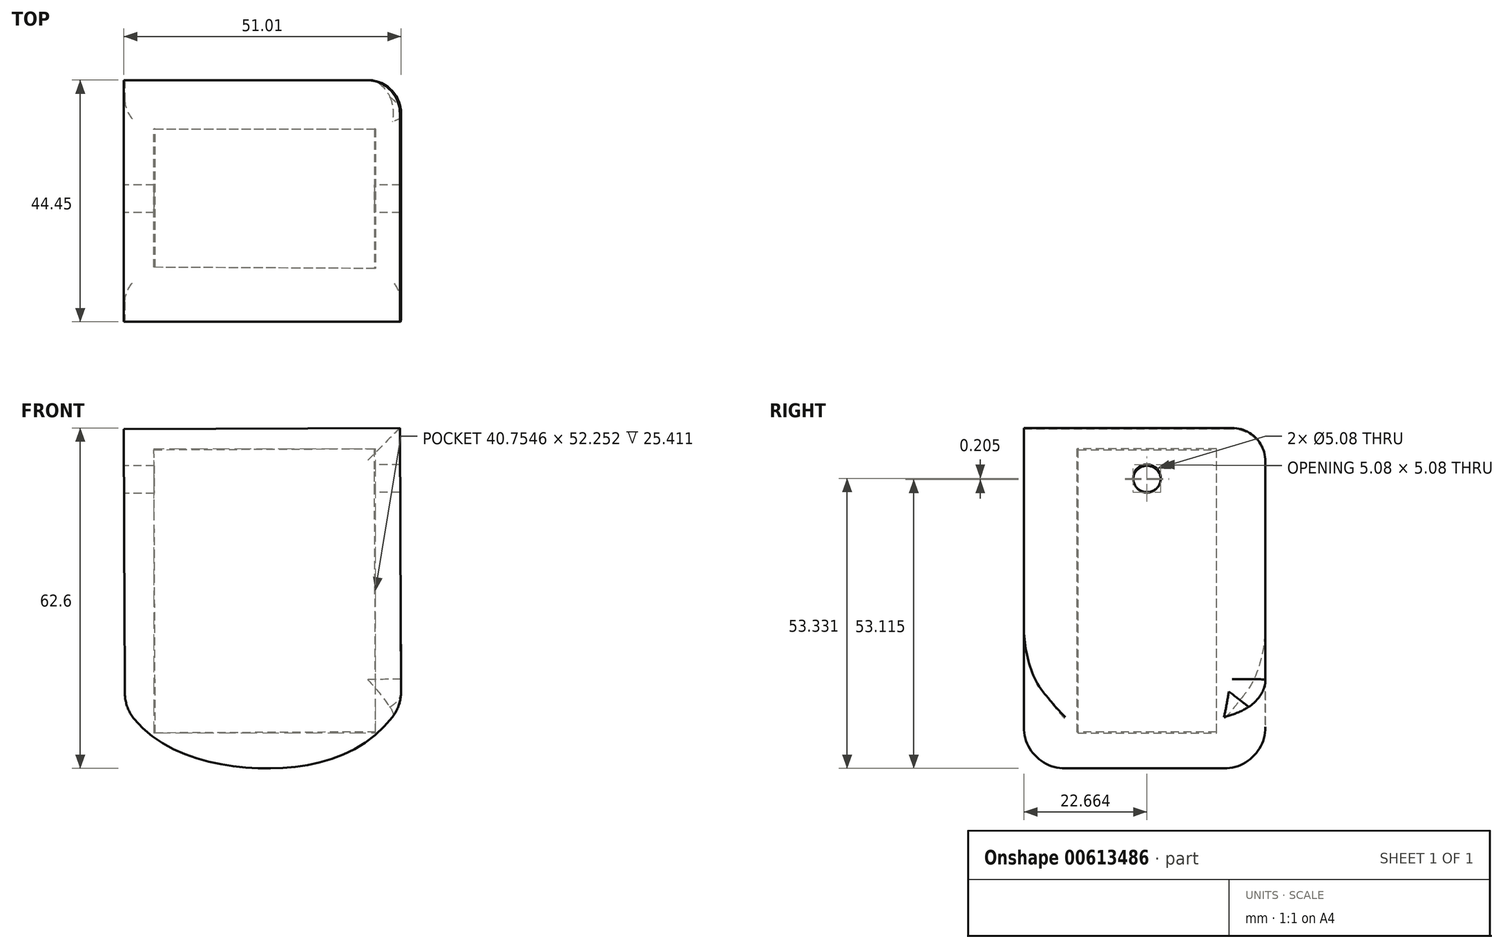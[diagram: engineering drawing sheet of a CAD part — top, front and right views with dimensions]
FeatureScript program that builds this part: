
annotation { "Feature Type Name" : "Feature", "Feature Type Description" : "" }
export const myFeature = defineFeature(function(context is Context, id is Id, definition is map)
    precondition{}
    {
        {
            var Q0;
            Q0=qCreatedBy(makeId("Front.planeOp"),FACE);
            var sketch = newSketch(context, id + "F0", { "sketchPlane" : qUnion([Q0])});
            skLineSegment(sketch, "E0", {"start": v(-36.95, 37.52) * mm, "end": v(-36.95, -63.62) * mm});
            skLineSegment(sketch, "E1", {"start": v(-36.95, -63.62) * mm, "end": v(64.65, -63.62) * mm});
            skLineSegment(sketch, "E2", {"start": v(64.65, -63.62) * mm, "end": v(64.65, 37.98) * mm});
            skLineSegment(sketch, "E3", {"start": v(64.65, 37.98) * mm, "end": v(-36.95, 37.52) * mm});
            skSolve(sketch);
        }
        {
            var Q0;
            Q0 = qSketchRegion(id + "F0", true);
            extrude(context, id + "F1", {"entities" : qUnion([Q0]), "depth" : 101.6 * mm, "offsetDistance" : 25.4 * mm});
        }
        {
            var Q0;
            Q0=makeQuery(id+"F1.opExtrude","CAP_FACE",FACE,{"disambiguationData":[OSD([sQuery(id+"F0.wireOp",EDGE,"E0"),sQuery(id+"F0.wireOp",EDGE,"E1"),sQuery(id+"F0.wireOp",EDGE,"E2"),sQuery(id+"F0.wireOp",EDGE,"E3")])],"isStart":false});
            var sketch = newSketch(context, id + "F2", { "sketchPlane" : qUnion([Q0])});
            skLineSegment(sketch, "E4", {"start": v(-11.05, 21.73) * mm, "end": v(39.75, 21.96) * mm});
            skLineSegment(sketch, "E5", {"start": v(39.75, 21.96) * mm, "end": v(39.98, -28.84) * mm});
            skLineSegment(sketch, "E6", {"start": v(39.98, -28.84) * mm, "end": v(-10.82, -29.07) * mm});
            skLineSegment(sketch, "E7", {"start": v(-10.82, -29.07) * mm, "end": v(-11.05, 21.73) * mm});
            skFitSpline(sketch, "E8", {"points": [v(-10.82, -29.07) * mm, v(14.1, -40.62) * mm, v(39.98, -28.84) * mm], "startDerivative": vector(27.81, -48.96) * mm, "endDerivative": vector(33.1, 55.47) * mm});
            skLineSegment(sketch, "E9", {"start": v(-36.95, 37.52) * mm, "end": v(64.65, 37.98) * mm});
            skLineSegment(sketch, "E10", {"start": v(64.65, 37.98) * mm, "end": v(64.65, -63.62) * mm});
            skLineSegment(sketch, "E11", {"start": v(64.65, -63.62) * mm, "end": v(-36.95, -63.62) * mm});
            skLineSegment(sketch, "E12", {"start": v(-36.95, -63.62) * mm, "end": v(-36.95, 37.52) * mm});
            skLineSegment(sketch, "E13", {"start": v(-11.05, 21.73) * mm, "end": v(-36.95, 37.52) * mm});
            skLineSegment(sketch, "E14", {"start": v(39.75, 21.96) * mm, "end": v(64.65, 37.98) * mm});
            skLineSegment(sketch, "E15", {"start": v(39.98, -28.84) * mm, "end": v(64.65, -63.62) * mm});
            skLineSegment(sketch, "E16", {"start": v(-10.82, -29.07) * mm, "end": v(-36.95, -63.62) * mm});
            skSolve(sketch);
        }
        {
            var Q0;
            Q0=makeQuery(id+"F2.imprint","IMPRINT",FACE,{"disambiguationData":[TD([[makeQuery(id+"F2.imprint","IMPRINT",EDGE,{"derivedFrom":sQuery(id+"F2.wireOp",EDGE,"E7")}),1.0]])]});
            var Q1;
            Q1=makeQuery(id+"F2.imprint","IMPRINT",FACE,{"disambiguationData":[TD([[makeQuery(id+"F2.imprint","IMPRINT",EDGE,{"derivedFrom":sQuery(id+"F2.wireOp",EDGE,"E4")}),1.0]])]});
            var Q2;
            Q2=makeQuery(id+"F2.imprint","IMPRINT",FACE,{"disambiguationData":[TD([[makeQuery(id+"F2.imprint","IMPRINT",EDGE,{"derivedFrom":sQuery(id+"F2.wireOp",EDGE,"E5")}),1.0]])]});
            var Q3;
            Q3=makeQuery(id+"F2.imprint","IMPRINT",FACE,{"disambiguationData":[TD([[makeQuery(id+"F2.imprint","IMPRINT",EDGE,{"derivedFrom":sQuery(id+"F2.wireOp",EDGE,"E8")}),-1.0]])]});
            extrude(context, id + "F3", {"entities" : qUnion([Q0, Q1, Q2, Q3]), "operationType" : NewBodyOperationType.REMOVE, "oppositeDirection" : true, "depth" : 101.6 * mm, "offsetDistance" : 25.4 * mm});
        }
        {
            var Q0;
            Q0=makeQuery(id+"F3.boolean.opBoolean","COPY",FACE,{"derivedFrom":makeQuery(id+"F3.opExtrude","SWEPT_FACE",FACE,{"disambiguationData":[OSD([sQuery(id+"F2.wireOp",EDGE,"E7")])]})});
            var sketch = newSketch(context, id + "F4", { "sketchPlane" : qUnion([Q0])});
            skLineSegment(sketch, "E17", {"start": v(57.15, 53.9) * mm, "end": v(57.15, -52.37) * mm});
            skLineSegment(sketch, "E18", {"start": v(57.15, -52.37) * mm, "end": v(-11.18, -52.37) * mm});
            skLineSegment(sketch, "E19", {"start": v(-11.18, -52.37) * mm, "end": v(-11.18, 54.37) * mm});
            skLineSegment(sketch, "E20", {"start": v(-11.18, 54.37) * mm, "end": v(57.15, 53.9) * mm});
            skSolve(sketch);
        }
        {
            var Q0;
            Q0 = qSketchRegion(id + "F4", true);
            extrude(context, id + "F5", {"entities" : qUnion([Q0]), "operationType" : NewBodyOperationType.REMOVE, "oppositeDirection" : true, "depth" : 101.6 * mm, "offsetDistance" : 25.4 * mm});
        }
        {
            var Q0;
            Q0=makeQuery(id+"F5.boolean.opBoolean","INTERSECT",EDGE,{"derivedFrom":[makeQuery(id+"F3.boolean.opBoolean","COPY",FACE,{"derivedFrom":makeQuery(id+"F3.opExtrude","SWEPT_FACE",FACE,{"disambiguationData":[OSD([sQuery(id+"F2.wireOp",EDGE,"E4")])]})}),makeQuery(id+"F5.opExtrude","SWEPT_FACE",FACE,{"disambiguationData":[OSD([sQuery(id+"F4.wireOp",EDGE,"E17")])]})]});
            var Q1;
            Q1=makeQuery(id+"F5.boolean.opBoolean","INTERSECT",EDGE,{"derivedFrom":[makeQuery(id+"F3.boolean.opBoolean","COPY",FACE,{"derivedFrom":makeQuery(id+"F3.opExtrude","SWEPT_FACE",FACE,{"disambiguationData":[OSD([sQuery(id+"F2.wireOp",EDGE,"E5")])]})}),makeQuery(id+"F5.opExtrude","SWEPT_FACE",FACE,{"disambiguationData":[OSD([sQuery(id+"F4.wireOp",EDGE,"E17")])]})]});
            var Q2;
            Q2=makeQuery(id+"F5.boolean.opBoolean","COPY",EDGE,{"derivedFrom":makeQuery(id+"F5.opExtrude","CAP_EDGE",EDGE,{"disambiguationData":[OSD([sQuery(id+"F4.wireOp",EDGE,"E17")])],"isStart":true})});
            var Q3;
            Q3=makeQuery(id+"F3.boolean.opBoolean","COPY",EDGE,{"derivedFrom":makeQuery(id+"F3.opExtrude","CAP_EDGE",EDGE,{"disambiguationData":[OSD([sQuery(id+"F2.wireOp",EDGE,"E5")])],"isStart":true})});
            var Q4;
            Q4=makeQuery(id+"F3.boolean.opBoolean","COPY",EDGE,{"derivedFrom":makeQuery(id+"F3.opExtrude","CAP_EDGE",EDGE,{"disambiguationData":[OSD([sQuery(id+"F2.wireOp",EDGE,"E4")])],"isStart":true})});
            var Q5;
            Q5=makeQuery(id+"F3.boolean.opBoolean","COPY",EDGE,{"derivedFrom":makeQuery(id+"F3.opExtrude","CAP_EDGE",EDGE,{"disambiguationData":[OSD([sQuery(id+"F2.wireOp",EDGE,"E7")])],"isStart":true})});
            fillet(context, id + "F6", {"entities" : qUnion([Q0, Q1, Q2, Q3, Q4, Q5]), "radius" : 6.13 * mm, "tangentPropagation" : true, "allowEdgeOverflow" : false});
        }
        {
            var Q0;
            Q0=makeQuery(id+"F5.boolean.opBoolean","INTERSECT",EDGE,{"derivedFrom":[makeQuery(id+"F3.boolean.opBoolean","COPY",FACE,{"derivedFrom":makeQuery(id+"F3.opExtrude","SWEPT_FACE",FACE,{"disambiguationData":[OSD([sQuery(id+"F2.wireOp",EDGE,"E8")])]})}),makeQuery(id+"F5.opExtrude","SWEPT_FACE",FACE,{"disambiguationData":[OSD([sQuery(id+"F4.wireOp",EDGE,"E17")])]})]});
            var Q1;
            Q1=makeQuery(id+"F3.boolean.opBoolean","COPY",FACE,{"derivedFrom":makeQuery(id+"F3.opExtrude","SWEPT_FACE",FACE,{"disambiguationData":[OSD([sQuery(id+"F2.wireOp",EDGE,"E8")])]})});
            fillet(context, id + "F7", {"entities" : qUnion([Q0, Q1]), "radius" : 7.62 * mm, "tangentPropagation" : true, "allowEdgeOverflow" : false});
        }
        {
            var Q0;
            Q0=makeQuery(id+"F3.boolean.opBoolean","COPY",FACE,{"derivedFrom":makeQuery(id+"F3.opExtrude","SWEPT_FACE",FACE,{"disambiguationData":[OSD([sQuery(id+"F2.wireOp",EDGE,"E4")])]})});
            var sketch = newSketch(context, id + "F8", { "sketchPlane" : qUnion([Q0])});
            skLineSegment(sketch, "E21", {"start": v(-5.4, -91.57) * mm, "end": v(-5.4, -66.15) * mm});
            skLineSegment(sketch, "E22", {"start": v(-5.4, -66.15) * mm, "end": v(35.12, -66.15) * mm});
            skLineSegment(sketch, "E23", {"start": v(35.12, -66.15) * mm, "end": v(35.12, -91.8) * mm});
            skLineSegment(sketch, "E24", {"start": v(35.12, -91.8) * mm, "end": v(-5.4, -91.57) * mm});
            skSolve(sketch);
        }
        {
            var Q0;
            Q0 = qSketchRegion(id + "F8", true);
            extrude(context, id + "F9", {"entities" : qUnion([Q0]), "operationType" : NewBodyOperationType.REMOVE, "oppositeDirection" : true, "depth" : 55.88 * mm, "offsetDistance" : 25.4 * mm});
        }
        {
            var Q0;
            Q0=makeQuery(id+"F3.boolean.opBoolean","COPY",FACE,{"derivedFrom":makeQuery(id+"F3.opExtrude","SWEPT_FACE",FACE,{"disambiguationData":[OSD([sQuery(id+"F2.wireOp",EDGE,"E4")])]})});
            var sketch = newSketch(context, id + "F10", { "sketchPlane" : qUnion([Q0])});
            skLineSegment(sketch, "E25", {"start": v(35.12, -91.8) * mm, "end": v(-5.4, -91.57) * mm});
            skLineSegment(sketch, "E26", {"start": v(-5.4, -91.57) * mm, "end": v(-5.4, -66.15) * mm});
            skLineSegment(sketch, "E27", {"start": v(-5.4, -66.15) * mm, "end": v(35.12, -66.15) * mm});
            skLineSegment(sketch, "E28", {"start": v(35.12, -66.15) * mm, "end": v(35.12, -91.8) * mm});
            skSolve(sketch);
        }
        {
            var Q0;
            Q0 = qSketchRegion(id + "F10", true);
            extrude(context, id + "F11", {"entities" : qUnion([Q0]), "operationType" : NewBodyOperationType.ADD, "oppositeDirection" : true, "depth" : 3.8 * mm, "offsetDistance" : 25.4 * mm});
        }
        {
            var Q0;
            Q0=makeQuery(id+"F3.boolean.opBoolean","COPY",FACE,{"derivedFrom":makeQuery(id+"F3.opExtrude","SWEPT_FACE",FACE,{"disambiguationData":[OSD([sQuery(id+"F2.wireOp",EDGE,"E7")])]})});
            var sketch = newSketch(context, id + "F12", { "sketchPlane" : qUnion([Q0])});
            skCircle(sketch, "E29", {"center": v(78.94, 12.51) * mm, "radius": 2.54 * mm});
            skSolve(sketch);
        }
        {
            var Q0;
            Q0=makeQuery(id+"F12.imprint","IMPRINT",FACE,{"disambiguationData":[TD([[makeQuery(id+"F12.imprint","IMPRINT",EDGE,{"derivedFrom":sQuery(id+"F12.wireOp",EDGE,"E29")}),1.0]])]});
            extrude(context, id + "F13", {"entities" : qUnion([Q0]), "operationType" : NewBodyOperationType.REMOVE, "oppositeDirection" : true, "depth" : 69.34 * mm, "offsetDistance" : 25.4 * mm});
        }
    });
